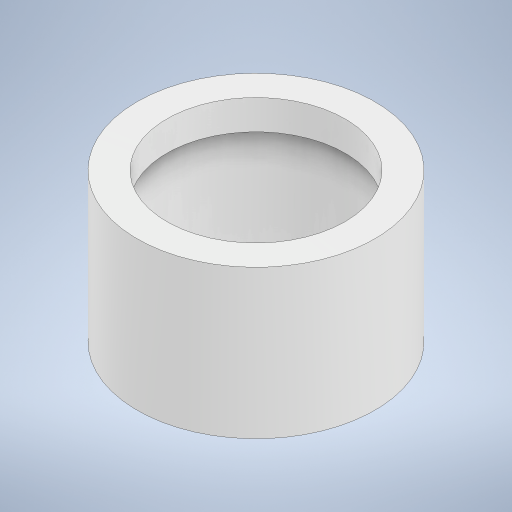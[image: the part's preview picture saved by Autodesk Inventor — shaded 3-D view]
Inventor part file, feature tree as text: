
AUTODESK INVENTOR PART (.ipt)
format: ipt  version: 2023 (Build 270158000, 158)  size: 236,544 bytes
history: native  units: mm
features: extrude x2, sketch x2
ambient origin geometry x8: Origin, YZ Plane, XZ Plane, XY Plane, X Axis, Y Axis, Z Axis, Center Point
bodies: Solid1 (feature_tree)
feature tree (4):
  extrude  "Extrusion1"  Depth=10.0mm
  extrude  "Extrusion2"  Depth=10.0mm
  sketch  "Sketch1"  dims[d0=160.0mm d1=10.0mm]
  sketch  "Sketch2"  dims[d2=100.0mm d3=0.0mm d4=10.0mm d5=20.0mm d6=0.0mm]
